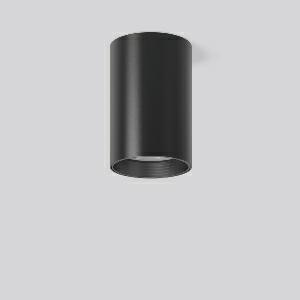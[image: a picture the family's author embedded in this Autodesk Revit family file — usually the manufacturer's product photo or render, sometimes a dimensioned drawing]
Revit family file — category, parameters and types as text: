
# Revit family: heledon_maxi_a_931222_003_1_76_1daf
name_source: partatom
category: Lighting Fixtures
units: mm (PartAtom-declared; Revit-internal decimal feet)

## family parameters
Cut with Voids When Loaded = No
Host = Face
Light Source = No
Part Type = Normal
Room Calculation Point = No
Round Connector Dimension = Use Diameter
Shared = No

## types (1)
- HELEDON maxi A (1 x LED Modul 940, 2950 lm, 4000)
    Apparent Load = 25 VA
    Approval mark = CE
    CIE Flux Codes = 96 100 100 100 100
    Color Rendering = 92
    Color Temperature = 4000
    Default Elevation = 1800 mm
    Description = Series: HELEDON maxi
Cylindrical surface-mounted downlight. Housing: die-cast aluminium, powder-coated. Internal ceiling frame polycarbonate with bayonet mounting. Black plastic ring and recessed LED to prevent glare from the side. Optical assembly with lens made of plastic (polycarbonate) for the best homogeneous light distribution - can be changed without tools. Best colour rendering index Ra>90. Suitable for Ceiling mounting. Easy installation with a separate ceiling frame with bayonet mounting and plug connection. Driver integrated. Connected via plug-in connector. High quality converter without flickering and stroboscopic effect. The following accessories can be mounted without use of tools: interchangeable lenses, decorative glasses, honeycomb louvre, clear and frosted diffusers, white interchangeable plastic ring. 
Colour: deep black, matt (RAL 9005)
Diameter: 123 mm
Height: 183 mm
Lamp: LED
Socket: without socket
Colour temperature: 4000K
Colour rendering index (CRI): 92
System power: 25 W
Rated luminous flux: 2950 lm
Luminous efficiency: 118 lm/W
Control gear: Converter, dimmable, DALI
Protection class: I
Type of protection: IP 20
    Height = 183 mm
    Lamp = 1 x LED Modul 940
    Lamp Light Flux = 2950 lm
    Lamp count = 1
    Length = 123 mm
    Lifetime = 50000 h
    Luminous efficacy = 118 lm/W
    Manufacturer = RZB
    ModVariant = No
    Model = 931222.003.1.76
    Mounting Place = Ceiling
    Mounting Type = Surface mounted
    Number of Poles = 1
    OnlyDefault = Yes
    Power Factor = 1
    Product Name = HELEDON maxi A
    Product group = Surface mounted downlights
    ProductGroupID = 302
    Protection Class = Protection class I
    Protection Degree = IP 20
    RLX_Detail_Level = 1
    RLX_Emergency_Light_Flux = 0 lm
    RLX_Emergency_Type = 0
    RLX_Emergency_Type_DB = No
    RlxData = <blob elided: 98021 chars, md5=dd5ac647>
    Socket = socket
    Standby Power = 0 W
    System Light Flux = 2950 lm
    System Power = 25 W
    Type Comments = Product without accessories
    Type Image = 931193.003.jpg
    URL = http://relux.com
    VarID = ---
    Voltage = 230 V
    Voltage Range = 220-240 V
    Weight = 0.00 kg
    Width = 0 mm  [stored 0 ft]

note: [stored X ft] marks values corroborated as IEEE doubles in the binary element streams (Revit-internal decimal feet)

## geometry (parser evidence)
native form markers: Blend x4, Sweep x11
no freeform markers — native parametric forms only
